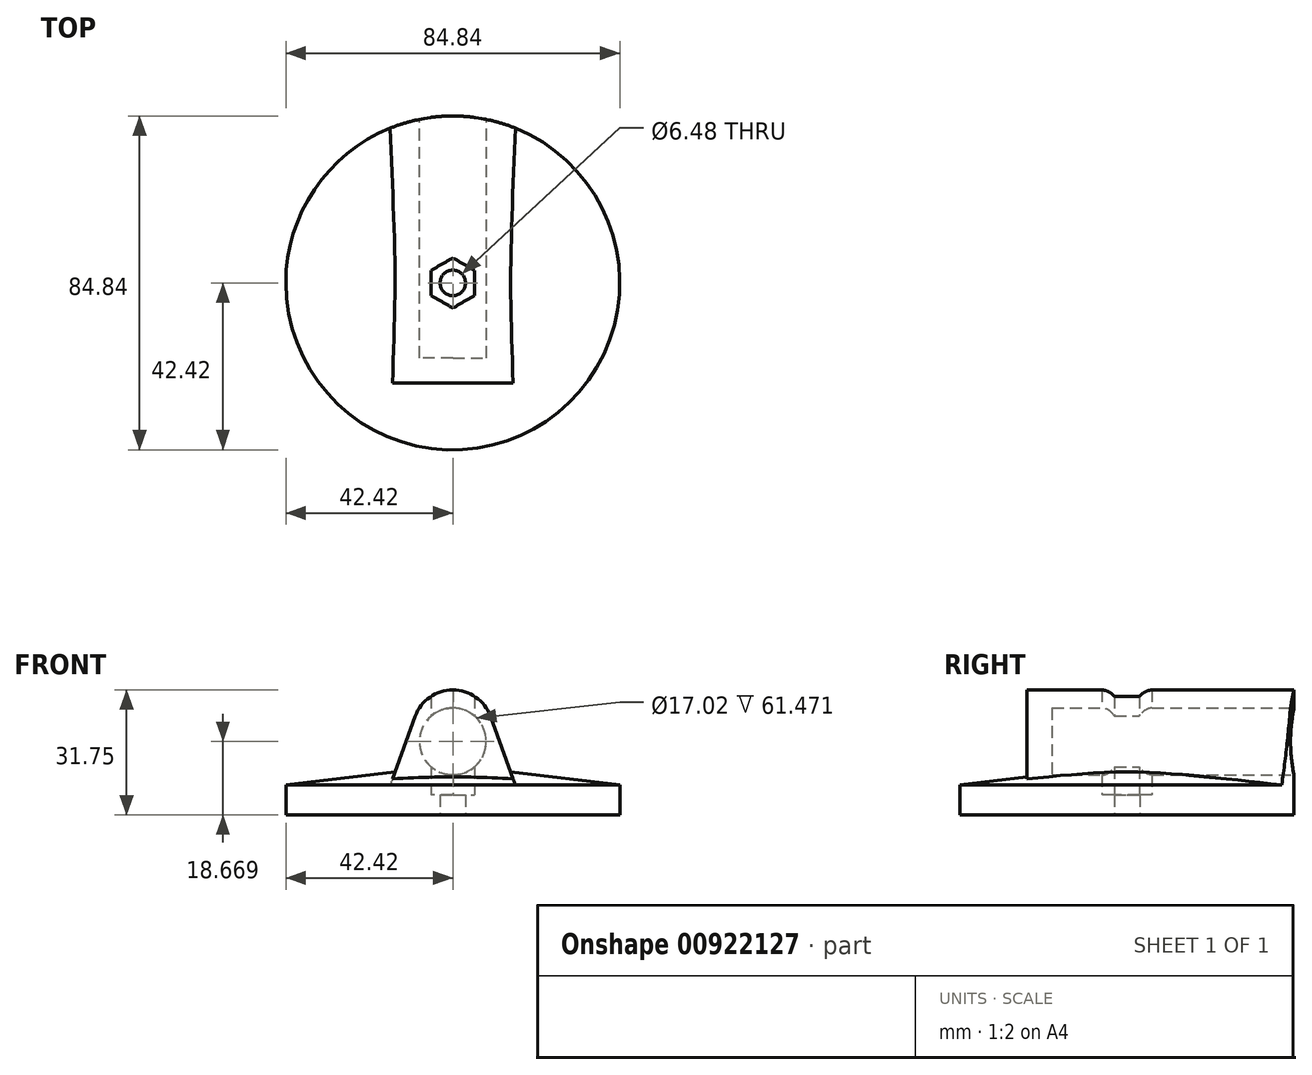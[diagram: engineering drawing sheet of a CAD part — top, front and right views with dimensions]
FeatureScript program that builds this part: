
annotation { "Feature Type Name" : "Feature", "Feature Type Description" : "" }
export const myFeature = defineFeature(function(context is Context, id is Id, definition is map)
    precondition{}
    {
        {
            var Q0;
            Q0=qCreatedBy(makeId("Front.planeOp"),FACE);
            var sketch = newSketch(context, id + "F0", { "sketchPlane" : qUnion([Q0])});
            skLineSegment(sketch, "E0", {"start": v(0, 0) * mm, "end": v(0, 12.7) * mm});
            skLineSegment(sketch, "E1", {"start": v(0, 12.7) * mm, "end": v(42.42, 7.62) * mm});
            skLineSegment(sketch, "E2", {"start": v(42.42, 7.62) * mm, "end": v(42.42, 0) * mm});
            skLineSegment(sketch, "E3", {"start": v(42.42, 0) * mm, "end": v(0, 0) * mm});
            skSolve(sketch);
        }
        {
            var Q0;
            Q0=makeQuery(id+"F0.imprint","IMPRINT",FACE,{"disambiguationData":[TD([[makeQuery(id+"F0.imprint","IMPRINT",EDGE,{"derivedFrom":sQuery(id+"F0.wireOp",EDGE,"E0")}),-1.0]])]});
            var Q1;
            Q1=sQuery(id+"F0.wireOp",EDGE,"E0");
            revolve(context, id + "F1", {"surfaceOperationType" : NewSurfaceOperationType.NEW, "entities" : qUnion([Q0]), "axis" : qUnion([Q1]), "revolveType" : RevolveType.FULL});
        }
        {
            var Q0;
            Q0=qCreatedBy(makeId("Front.planeOp"),FACE);
            var sketch = newSketch(context, id + "F2", { "sketchPlane" : qUnion([Q0])});
            skLineSegment(sketch, "E4", {"start": v(9.55, 25.06) * mm, "end": v(18.67, 0) * mm});
            skLineSegment(sketch, "E5", {"start": v(18.67, 0) * mm, "end": v(-18.67, 0) * mm});
            skLineSegment(sketch, "E6", {"start": v(-18.67, 0) * mm, "end": v(-9.55, 25.06) * mm});
            skArc(sketch, "E7", {"start": v(9.55, 25.06) * mm, "mid": v(0, 31.75) * mm, "end": v(-9.55, 25.06) * mm});
            skSolve(sketch);
        }
        {
            var Q0;
            Q0=makeQuery(id+"F2.imprint","IMPRINT",FACE,{"disambiguationData":[TD([[makeQuery(id+"F2.imprint","IMPRINT",EDGE,{"derivedFrom":sQuery(id+"F2.wireOp",EDGE,"E4")}),-1.0]])]});
            var Q1;
            Q1=makeQuery(id+"F1.opRevolve","SWEPT_FACE",FACE,{"disambiguationData":[OSD([sQuery(id+"F0.wireOp",EDGE,"E2")])]});
            extrude(context, id + "F3", {"entities" : qUnion([Q0]), "operationType" : NewBodyOperationType.ADD, "depth" : 25.4 * mm, "offsetDistance" : 25.4 * mm, "hasSecondDirection" : true, "secondDirectionBound" : SecondDirectionBoundingType.UP_TO_SURFACE, "secondDirectionOppositeDirection" : true, "secondDirectionDepth" : 25.4 * mm, "secondDirectionBoundEntityFace" : qUnion([Q1])});
        }
        {
            var Q0;
            Q0=qCreatedBy(makeId("Front.planeOp"),FACE);
            var sketch = newSketch(context, id + "F4", { "sketchPlane" : qUnion([Q0])});
            skCircle(sketch, "E8", {"center": v(0, 18.67) * mm, "radius": 8.5 * mm});
            skSolve(sketch);
        }
        {
            var Q0;
            Q0 = qSketchRegion(id + "F4", true);
            var Q1;
            {var subQ0=makeQuery(id+"F1.opRevolve","SWEPT_FACE",FACE,{"disambiguationData":[OSD([sQuery(id+"F0.wireOp",EDGE,"E2")])]});Q1=makeQuery(id+"F3.boolean.opBoolean","MERGE",FACE,{"derivedFrom":[subQ0,makeQuery(id+"F3.opExtrude","CAP_FACE",FACE,{"disambiguationData":[OSD([sQuery(id+"F2.wireOp",EDGE,"E4"),sQuery(id+"F2.wireOp",EDGE,"E5"),sQuery(id+"F2.wireOp",EDGE,"E6"),sQuery(id+"F2.wireOp",EDGE,"E7")]),topologyDisambiguationEdgeConnected([subQ0])],"isStart":false})]});}
            extrude(context, id + "F5", {"entities" : qUnion([Q0]), "operationType" : NewBodyOperationType.REMOVE, "depth" : 19.05 * mm, "offsetDistance" : 25.4 * mm, "hasSecondDirection" : true, "secondDirectionBound" : SecondDirectionBoundingType.UP_TO_SURFACE, "secondDirectionOppositeDirection" : true, "secondDirectionDepth" : 25.4 * mm, "secondDirectionBoundEntityFace" : qUnion([Q1])});
        }
        {
            var Q0;
            Q0=makeQuery(id+"F1.opRevolve","SWEPT_FACE",FACE,{"disambiguationData":[OSD([sQuery(id+"F0.wireOp",EDGE,"E3")])]});
            var sketch = newSketch(context, id + "F6", { "sketchPlane" : qUnion([Q0])});
            skCircle(sketch, "E9", {"center": v(0, 0) * mm, "radius": 3.24 * mm});
            skSolve(sketch);
        }
        {
            var Q0;
            Q0 = qSketchRegion(id + "F6", true);
            extrude(context, id + "F7", {"entities" : qUnion([Q0]), "operationType" : NewBodyOperationType.REMOVE, "oppositeDirection" : true, "depth" : 5.08 * mm, "offsetDistance" : 25.4 * mm});
        }
        {
            var Q0;
            Q0=makeQuery(id+"F7.boolean.opBoolean","COPY",FACE,{"derivedFrom":makeQuery(id+"F7.opExtrude","CAP_FACE",FACE,{"disambiguationData":[OSD([sQuery(id+"F6.wireOp",EDGE,"E9")])],"isStart":false})});
            var sketch = newSketch(context, id + "F8", { "sketchPlane" : qUnion([Q0])});
            skCircle(sketch, "E10.cCircle", {"center": v(0, 0) * mm, "radius": 5.52 * mm, "construction": true});
            skLineSegment(sketch, "E10.0", {"start": v(5.52, -3.19) * mm, "end": v(0, -6.38) * mm});
            skLineSegment(sketch, "E10.1", {"start": v(0, -6.38) * mm, "end": v(-5.52, -3.19) * mm});
            skLineSegment(sketch, "E10.2", {"start": v(-5.52, -3.19) * mm, "end": v(-5.52, 3.19) * mm});
            skLineSegment(sketch, "E10.3", {"start": v(-5.52, 3.19) * mm, "end": v(0, 6.38) * mm});
            skLineSegment(sketch, "E10.4", {"start": v(0, 6.38) * mm, "end": v(5.52, 3.19) * mm});
            skLineSegment(sketch, "E10.5", {"start": v(5.52, 3.19) * mm, "end": v(5.52, -3.19) * mm});
            skPoint(sketch, "E10.0.midPoint", {"position": v(2.76, -4.78) * mm});
            skSolve(sketch);
        }
        {
            var Q0;
            Q0 = qSketchRegion(id + "F8", true);
            extrude(context, id + "F9", {"entities" : qUnion([Q0]), "operationType" : NewBodyOperationType.REMOVE, "oppositeDirection" : true, "depth" : 50.8 * mm, "offsetDistance" : 25.4 * mm});
        }
    });
